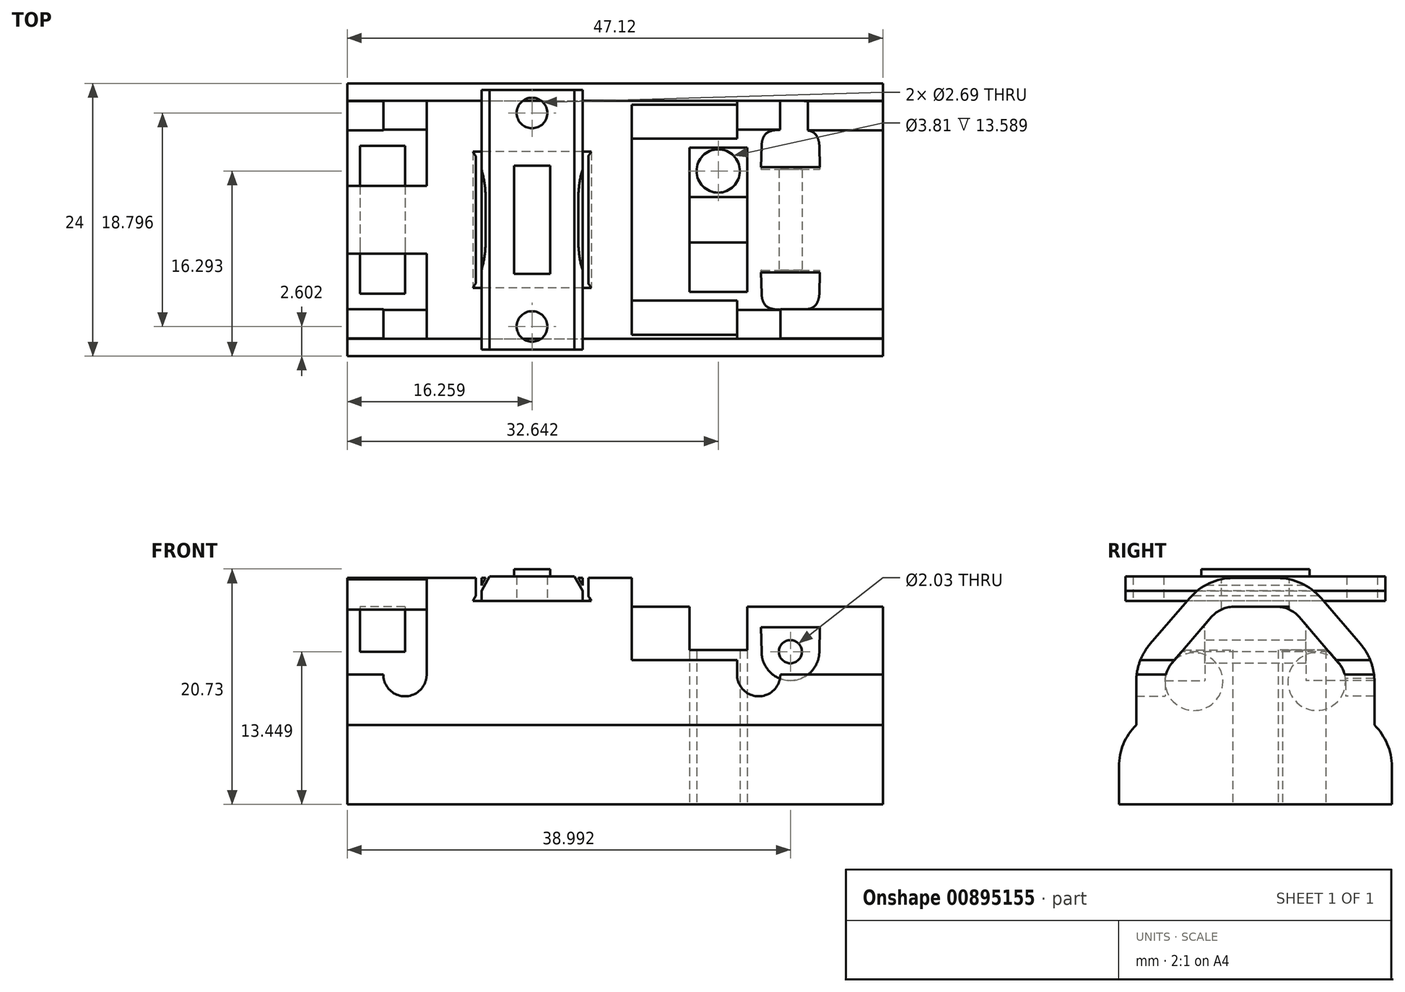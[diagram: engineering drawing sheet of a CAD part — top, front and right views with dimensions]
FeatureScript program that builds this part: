
annotation { "Feature Type Name" : "Feature", "Feature Type Description" : "" }
export const myFeature = defineFeature(function(context is Context, id is Id, definition is map)
    precondition{}
    {
        {
            var Q0;
            Q0=qCreatedBy(makeId("Right.planeOp"),FACE);
            var sketch = newSketch(context, id + "F0", { "sketchPlane" : qUnion([Q0])});
            skLineSegment(sketch, "E0.bottom", {"start": v(0, 0) * mm, "end": v(12, 0) * mm});
            skLineSegment(sketch, "E0.top", {"start": v(10.48, 6.99) * mm, "end": v(12, 6.99) * mm});
            skLineSegment(sketch, "E0.left", {"start": v(0, 0) * mm, "end": v(0, 6.99) * mm});
            skLineSegment(sketch, "E0.right", {"start": v(12, 0) * mm, "end": v(12, 6.99) * mm});
            skLineSegment(sketch, "E1.bottom", {"start": v(0, 0) * mm, "end": v(10.48, 0) * mm});
            skLineSegment(sketch, "E1.top", {"start": v(0, 19.94) * mm, "end": v(4.25, 19.94) * mm});
            skLineSegment(sketch, "E1.left", {"start": v(0, 0) * mm, "end": v(0, 19.94) * mm});
            skLineSegment(sketch, "E1.right", {"start": v(10.48, 6.99) * mm, "end": v(10.48, 12.7) * mm});
            skLineSegment(sketch, "E2", {"start": v(4.25, 19.94) * mm, "end": v(10.48, 12.7) * mm});
            skSolve(sketch);
        }
        {
            var Q0;
            Q0=qSketchRegion(id+"F0",true);
            extrude(context, id + "F1", {"entities" : qUnion([Q0]), "oppositeDirection" : true, "depth" : 47.12 * mm, "offsetDistance" : 25.4 * mm});
        }
        {
            var Q0;
            Q0=makeQuery(id+"F1.opExtrude","SWEPT_EDGE",EDGE,{"disambiguationData":[OSD([sQuery(id+"F0.wireOp",EDGE,"E1.top"),sQuery(id+"F0.wireOp",EDGE,"E2")])]});
            var Q1;
            Q1=makeQuery(id+"F1.opExtrude","SWEPT_EDGE",EDGE,{"disambiguationData":[OSD([sQuery(id+"F0.wireOp",EDGE,"E1.right"),sQuery(id+"F0.wireOp",EDGE,"E2")])]});
            var Q2;
            Q2=makeQuery(id+"F1.opExtrude","SWEPT_EDGE",EDGE,{"disambiguationData":[OSD([sQuery(id+"F0.wireOp",EDGE,"E0.top"),sQuery(id+"F0.wireOp",EDGE,"E0.right")])]});
            fillet(context, id + "F2", {"entities" : qUnion([Q0, Q1, Q2]), "radius" : 5.08 * mm, "tangentPropagation" : true, "allowEdgeOverflow" : false});
        }
        {
            var Q0;
            Q0=makeQuery(id+"F1.opExtrude","CAP_FACE",FACE,{"disambiguationData":[OSD([sQuery(id+"F0.wireOp",EDGE,"E0.bottom"),sQuery(id+"F0.wireOp",EDGE,"E0.top"),sQuery(id+"F0.wireOp",EDGE,"E0.right"),sQuery(id+"F0.wireOp",EDGE,"E1.bottom"),sQuery(id+"F0.wireOp",EDGE,"E1.top"),sQuery(id+"F0.wireOp",EDGE,"E1.left"),sQuery(id+"F0.wireOp",EDGE,"E1.right"),sQuery(id+"F0.wireOp",EDGE,"E2")])],"isStart":true});
            var Q1;
            Q1=makeQuery(id+"F1.opExtrude","SWEPT_FACE",FACE,{"disambiguationData":[OSD([sQuery(id+"F0.wireOp",EDGE,"E1.left")])]});
            var Q2;
            Q2=makeQuery(id+"F1.opExtrude","CAP_FACE",FACE,{"disambiguationData":[OSD([sQuery(id+"F0.wireOp",EDGE,"E0.bottom"),sQuery(id+"F0.wireOp",EDGE,"E0.top"),sQuery(id+"F0.wireOp",EDGE,"E0.right"),sQuery(id+"F0.wireOp",EDGE,"E1.bottom"),sQuery(id+"F0.wireOp",EDGE,"E1.top"),sQuery(id+"F0.wireOp",EDGE,"E1.left"),sQuery(id+"F0.wireOp",EDGE,"E1.right"),sQuery(id+"F0.wireOp",EDGE,"E2")])],"isStart":false});
            var Q3;
            Q3=makeQuery(id+"F1.opExtrude","SWEPT_FACE",FACE,{"disambiguationData":[OSD([sQuery(id+"F0.wireOp",EDGE,"E0.bottom"),sQuery(id+"F0.wireOp",EDGE,"E1.bottom")])]});
            shell(context, id + "F3", {"entities" : qUnion([Q0, Q1, Q2, Q3]), "thickness" : 2.54 * mm});
        }
        {
            var Q0;
            Q0=qCreatedBy(makeId("Front.planeOp"),FACE);
            var sketch = newSketch(context, id + "F4", { "sketchPlane" : qUnion([Q0])});
            skLineSegment(sketch, "E3.bottom", {"start": v(0, 12.7) * mm, "end": v(-22.1, 12.7) * mm});
            skLineSegment(sketch, "E3.top", {"start": v(0, 25.4) * mm, "end": v(-22.1, 25.4) * mm});
            skLineSegment(sketch, "E3.left", {"start": v(0, 12.7) * mm, "end": v(0, 25.4) * mm});
            skLineSegment(sketch, "E3.right", {"start": v(-22.1, 12.7) * mm, "end": v(-22.1, 25.4) * mm});
            skSolve(sketch);
        }
        {
            var Q0;
            Q0=qSketchRegion(id+"F4",true);
            extrude(context, id + "F5", {"entities" : qUnion([Q0]), "operationType" : NewBodyOperationType.REMOVE, "oppositeDirection" : true, "depth" : 25.4 * mm, "offsetDistance" : 25.4 * mm});
        }
        {
            var Q0;
            Q0=qCreatedBy(makeId("Front.planeOp"),FACE);
            var sketch = newSketch(context, id + "F6", { "sketchPlane" : qUnion([Q0])});
            skArc(sketch, "E4", {"start": v(-12.83, 11.43) * mm, "mid": v(-10.92, 9.53) * mm, "end": v(-9.02, 11.43) * mm});
            skLineSegment(sketch, "E5.bottom", {"start": v(-9.02, 11.43) * mm, "end": v(0, 11.43) * mm});
            skLineSegment(sketch, "E5.top", {"start": v(-10.92, 17.78) * mm, "end": v(0, 17.78) * mm});
            skLineSegment(sketch, "E5.left", {"start": v(-10.92, 13.34) * mm, "end": v(-10.92, 17.78) * mm});
            skLineSegment(sketch, "E5.right", {"start": v(0, 11.43) * mm, "end": v(0, 17.78) * mm});
            skLineSegment(sketch, "E6", {"start": v(-10.92, 17.78) * mm, "end": v(-12.83, 17.78) * mm});
            skLineSegment(sketch, "E7", {"start": v(-12.83, 17.78) * mm, "end": v(-12.83, 11.43) * mm});
            skSolve(sketch);
        }
        {
            var Q0;
            Q0=qSketchRegion(id+"F6",true);
            extrude(context, id + "F7", {"entities" : qUnion([Q0]), "operationType" : NewBodyOperationType.REMOVE, "oppositeDirection" : true, "depth" : 25.4 * mm, "offsetDistance" : 25.4 * mm});
        }
        {
            var Q0;
            Q0=qCreatedBy(makeId("Front.planeOp"),FACE);
            cPlane(context, id + "F8", {"entities" : qUnion([Q0]), "cplaneType" : CPlaneType.OFFSET, "offset" : 2.98 * mm, "oppositeDirection" : true, "width" : 152.4 * mm, "height" : 152.4 * mm});
        }
        {
            var Q0;
            Q0=qCreatedBy(id+"F8.planeOp",FACE);
            var sketch = newSketch(context, id + "F9", { "sketchPlane" : qUnion([Q0])});
            skPoint(sketch, "E8.0", {"position": v(-10.92, 9.53) * mm});
            skLineSegment(sketch, "E9.0", {"start": v(0, 11.43) * mm, "end": v(-9.02, 11.43) * mm});
            skArc(sketch, "E10.0", {"start": v(-9.12, 10.82) * mm, "mid": v(-10.92, 9.53) * mm, "end": v(-12.73, 10.82) * mm});
            skArc(sketch, "E11", {"start": v(-43.94, 11.43) * mm, "mid": v(-42.04, 9.53) * mm, "end": v(-40.13, 11.43) * mm});
            skPoint(sketch, "E12.0", {"position": v(-47.12, 18.67) * mm});
            skLineSegment(sketch, "E13.0", {"start": v(-47.12, 17.4) * mm, "end": v(-47.12, 19.94) * mm});
            skLineSegment(sketch, "E14.bottom", {"start": v(-43.94, 11.43) * mm, "end": v(-47.12, 11.43) * mm});
            skLineSegment(sketch, "E14.top", {"start": v(-42.04, 19.94) * mm, "end": v(-47.12, 19.94) * mm});
            skLineSegment(sketch, "E14.left", {"start": v(-42.04, 11.43) * mm, "end": v(-42.04, 19.94) * mm});
            skLineSegment(sketch, "E14.right", {"start": v(-47.12, 11.43) * mm, "end": v(-47.12, 19.94) * mm});
            skLineSegment(sketch, "E15.top", {"start": v(-42.04, 19.94) * mm, "end": v(-40.13, 19.94) * mm});
            skLineSegment(sketch, "E15.right", {"start": v(-40.13, 11.43) * mm, "end": v(-40.13, 19.94) * mm});
            skSolve(sketch);
        }
        {
            var Q0;
            Q0=qSketchRegion(id+"F9",true);
            extrude(context, id + "F10", {"entities" : qUnion([Q0]), "operationType" : NewBodyOperationType.REMOVE, "oppositeDirection" : true, "depth" : 25.4 * mm, "offsetDistance" : 25.4 * mm});
        }
        {
            var Q0;
            Q0=qCreatedBy(makeId("Front.planeOp"),FACE);
            var sketch = newSketch(context, id + "F11", { "sketchPlane" : qUnion([Q0])});
            skLineSegment(sketch, "E16.0", {"start": v(-47.12, 19.94) * mm, "end": v(-22.1, 19.94) * mm});
            skLineSegment(sketch, "E17.0", {"start": v(-22.1, 17.4) * mm, "end": v(-22.1, 19.94) * mm});
            skLineSegment(sketch, "E18", {"start": v(-25.65, 17.9) * mm, "end": v(-36.07, 17.9) * mm});
            skLineSegment(sketch, "E19", {"start": v(-36.07, 17.9) * mm, "end": v(-34.94, 19.94) * mm});
            skLineSegment(sketch, "E20", {"start": v(-34.94, 19.94) * mm, "end": v(-26.78, 19.94) * mm});
            skLineSegment(sketch, "E21", {"start": v(-26.78, 19.94) * mm, "end": v(-25.65, 17.9) * mm});
            skLineSegment(sketch, "E22.0", {"start": v(0, 5.69) * mm, "end": v(0, 10.82) * mm});
            skSolve(sketch);
        }
        {
            var Q0;
            Q0=qSketchRegion(id+"F11",true);
            extrude(context, id + "F12", {"entities" : qUnion([Q0]), "operationType" : NewBodyOperationType.REMOVE, "oppositeDirection" : true, "depth" : 25.4 * mm, "offsetDistance" : 25.4 * mm});
        }
        {
            var Q0;
            Q0=makeQuery(id+"F1.opExtrude","SWEPT_BODY",BODY,{"disambiguationData":[OSD([sQuery(id+"F0.wireOp",EDGE,"E0.bottom"),sQuery(id+"F0.wireOp",EDGE,"E0.top"),sQuery(id+"F0.wireOp",EDGE,"E0.right"),sQuery(id+"F0.wireOp",EDGE,"E1.bottom"),sQuery(id+"F0.wireOp",EDGE,"E1.top"),sQuery(id+"F0.wireOp",EDGE,"E1.left"),sQuery(id+"F0.wireOp",EDGE,"E1.right"),sQuery(id+"F0.wireOp",EDGE,"E2")])]});
            var Q1;
            Q1=qCreatedBy(makeId("Front.planeOp"),FACE);
            mirror(context, id + "F13", {"operationType" : NewBodyOperationType.ADD, "entities" : qUnion([Q0]), "mirrorPlane" : qUnion([Q1])});
        }
        {
            var Q0;
            Q0=qCreatedBy(makeId("Right.planeOp"),FACE);
            var sketch = newSketch(context, id + "F14", { "sketchPlane" : qUnion([Q0])});
            skLineSegment(sketch, "E23.0", {"start": v(1.92, 17.4) * mm, "end": v(0, 17.4) * mm});
            skArc(sketch, "E24.0", {"start": v(1.92, 17.4) * mm, "mid": v(2.98, 17.17) * mm, "end": v(3.85, 16.51) * mm});
            skLineSegment(sketch, "E25.0", {"start": v(7.13, 12.7) * mm, "end": v(3.85, 16.51) * mm});
            skArc(sketch, "E26.0", {"start": v(7.86, 11.43) * mm, "mid": v(7.65, 11.98) * mm, "end": v(7.32, 12.47) * mm});
            skLineSegment(sketch, "E27.0", {"start": v(7.13, 12.7) * mm, "end": v(7.32, 12.47) * mm});
            skArc(sketch, "E28.0", {"start": v(7.94, 10.82) * mm, "mid": v(7.92, 11.13) * mm, "end": v(7.86, 11.43) * mm});
            skLineSegment(sketch, "E29.0", {"start": v(7.94, 5.69) * mm, "end": v(7.94, 10.82) * mm});
            skArc(sketch, "E30.0", {"start": v(9.46, 3.36) * mm, "mid": v(9.05, 4.75) * mm, "end": v(7.94, 5.69) * mm});
            skLineSegment(sketch, "E31.0", {"start": v(9.46, 0) * mm, "end": v(9.46, 3.36) * mm});
            skLineSegment(sketch, "E32", {"start": v(9.46, 0) * mm, "end": v(0, 0) * mm});
            skLineSegment(sketch, "E33", {"start": v(0, 0) * mm, "end": v(0, 17.4) * mm});
            skPoint(sketch, "E34.orphan", {"position": v(-1.92, 17.4) * mm});
            skSolve(sketch);
        }
        {
            var Q0;
            Q0=qSketchRegion(id+"F14",true);
            var Q1;
            {var subQ0=sQuery(id+"F0.wireOp",EDGE,"E0.right");var subQ1=sQuery(id+"F0.wireOp",EDGE,"E0.top");var subQ2=sQuery(id+"F0.wireOp",EDGE,"E1.right");var subQ3=sQuery(id+"F0.wireOp",EDGE,"E1.bottom");var subQ4=sQuery(id+"F0.wireOp",EDGE,"E0.bottom");var subQ5=sQuery(id+"F0.wireOp",EDGE,"E2");Q1=makeQuery(id+"F10.boolean.opBoolean","SPLIT",FACE,{"disambiguationData":[TD([makeQuery(id+"F1.opExtrude","SWEPT_FACE",FACE,{"disambiguationData":[OSD([subQ0])]})])],"derivedFrom":makeQuery(id+"F1.opExtrude","CAP_FACE",FACE,{"disambiguationData":[OSD([subQ4,subQ1,subQ0,subQ3,sQuery(id+"F0.wireOp",EDGE,"E1.top"),sQuery(id+"F0.wireOp",EDGE,"E1.left"),subQ2,subQ5])],"isStart":false})});}
            extrude(context, id + "F15", {"entities" : qUnion([Q0]), "endBound" : BoundingType.UP_TO_SURFACE, "oppositeDirection" : true, "depth" : 25.4 * mm, "endBoundEntityFace" : qUnion([Q1]), "offsetDistance" : 25.4 * mm});
        }
        {
            var Q0;
            Q0=qCreatedBy(makeId("Front.planeOp"),FACE);
            var sketch = newSketch(context, id + "F16", { "sketchPlane" : qUnion([Q0])});
            skLineSegment(sketch, "E35.0", {"start": v(-40.13, 14.13) * mm, "end": v(-40.13, 18.17) * mm});
            skLineSegment(sketch, "E36.left", {"start": v(-46, 17.4) * mm, "end": v(-46, 13.44) * mm});
            skLineSegment(sketch, "E36.right", {"start": v(-42.04, 17.4) * mm, "end": v(-42.04, 13.44) * mm});
            skLineSegment(sketch, "E37.0", {"start": v(-46, 17.4) * mm, "end": v(-42.04, 17.4) * mm});
            skLineSegment(sketch, "E38", {"start": v(-46.1, 17.4) * mm, "end": v(-42.04, 17.4) * mm});
            skPoint(sketch, "E39.orphan", {"position": v(-47.12, 17.4) * mm});
            skLineSegment(sketch, "E40.trimOffspring", {"start": v(-40.13, 17.4) * mm, "end": v(0, 17.4) * mm});
            skLineSegment(sketch, "E41", {"start": v(-46, 13.44) * mm, "end": v(-42.04, 13.44) * mm});
            skSolve(sketch);
        }
        {
            var Q0;
            Q0=qSketchRegion(id+"F16",true);
            extrude(context, id + "F17", {"entities" : qUnion([Q0]), "operationType" : NewBodyOperationType.REMOVE, "oppositeDirection" : true, "depth" : 25.4 * mm, "offsetDistance" : 25.4 * mm});
        }
        {
            var Q0;
            Q0=qCreatedBy(makeId("Front.planeOp"),FACE);
            var sketch = newSketch(context, id + "F18", { "sketchPlane" : qUnion([Q0])});
            skLineSegment(sketch, "E42.bottom", {"start": v(-17.02, 19.94) * mm, "end": v(-11.94, 19.94) * mm});
            skLineSegment(sketch, "E42.top", {"start": v(-17.02, 13.59) * mm, "end": v(-11.94, 13.59) * mm});
            skLineSegment(sketch, "E42.left", {"start": v(-17.02, 19.94) * mm, "end": v(-17.02, 13.59) * mm});
            skLineSegment(sketch, "E42.right", {"start": v(-11.94, 19.94) * mm, "end": v(-11.94, 13.59) * mm});
            skSolve(sketch);
        }
        {
            var Q0;
            Q0=qSketchRegion(id+"F18",true);
            extrude(context, id + "F19", {"entities" : qUnion([Q0]), "operationType" : NewBodyOperationType.REMOVE, "oppositeDirection" : true, "depth" : 25.4 * mm, "offsetDistance" : 25.4 * mm});
        }
        {
            var Q0;
            Q0=qCreatedBy(makeId("Front.planeOp"),FACE);
            var sketch = newSketch(context, id + "F20", { "sketchPlane" : qUnion([Q0])});
            skCircle(sketch, "E43", {"center": v(-8.13, 13.45) * mm, "radius": 1.02 * mm});
            skSolve(sketch);
        }
        {
            var Q0;
            Q0=qSketchRegion(id+"F20",true);
            extrude(context, id + "F21", {"entities" : qUnion([Q0]), "operationType" : NewBodyOperationType.REMOVE, "oppositeDirection" : true, "depth" : 25.4 * mm, "offsetDistance" : 25.4 * mm});
        }
        {
            var Q0;
            Q0=qCreatedBy(makeId("Front.planeOp"),FACE);
            cPlane(context, id + "F22", {"entities" : qUnion([Q0]), "cplaneType" : CPlaneType.OFFSET, "offset" : 4.44 * mm, "oppositeDirection" : true, "width" : 152.4 * mm, "height" : 152.4 * mm});
        }
        {
            var Q0;
            Q0=qCreatedBy(id+"F22.planeOp",FACE);
            var sketch = newSketch(context, id + "F23", { "sketchPlane" : qUnion([Q0])});
            skCircle(sketch, "E44.0", {"center": v(-8.13, 13.45) * mm, "radius": 1.02 * mm});
            skArc(sketch, "E45", {"start": v(-10.67, 13.4) * mm, "mid": v(-8.13, 10.9) * mm, "end": v(-5.59, 13.4) * mm});
            skLineSegment(sketch, "E46", {"start": v(-10.7, 15.6) * mm, "end": v(-5.55, 15.6) * mm});
            skLineSegment(sketch, "E47", {"start": v(-5.59, 13.4) * mm, "end": v(-5.55, 15.6) * mm});
            skLineSegment(sketch, "E48", {"start": v(-10.67, 13.4) * mm, "end": v(-10.7, 15.6) * mm});
            skSolve(sketch);
        }
        {
            var Q0;
            Q0=qSketchRegion(id+"F23",true);
            extrude(context, id + "F24", {"entities" : qUnion([Q0]), "operationType" : NewBodyOperationType.REMOVE, "oppositeDirection" : true, "depth" : 25.4 * mm, "offsetDistance" : 25.4 * mm});
        }
        {
            var Q0;
            Q0=qCreatedBy(makeId("Top.planeOp"),FACE);
            var sketch = newSketch(context, id + "F25", { "sketchPlane" : qUnion([Q0])});
            skLineSegment(sketch, "E49.0", {"start": v(-17.02, 6.36) * mm, "end": v(-11.94, 6.36) * mm});
            skLineSegment(sketch, "E50.0", {"start": v(-11.94, 1.92) * mm, "end": v(-11.94, 0) * mm});
            skLineSegment(sketch, "E51.0", {"start": v(-17.02, 1.92) * mm, "end": v(-17.02, 0) * mm});
            skLineSegment(sketch, "E52.0", {"start": v(-17.02, 0) * mm, "end": v(-11.94, 0) * mm});
            skLineSegment(sketch, "E53.bottom", {"start": v(-11.94, 0) * mm, "end": v(-17.02, 0) * mm});
            skLineSegment(sketch, "E53.top", {"start": v(-11.94, 2) * mm, "end": v(-17.02, 2) * mm});
            skLineSegment(sketch, "E53.left", {"start": v(-11.94, 0) * mm, "end": v(-11.94, 2) * mm});
            skLineSegment(sketch, "E53.right", {"start": v(-17.02, 0) * mm, "end": v(-17.02, 2) * mm});
            skSolve(sketch);
        }
        {
            var Q0;
            Q0=qSketchRegion(id+"F25",true);
            extrude(context, id + "F26", {"entities" : qUnion([Q0]), "operationType" : NewBodyOperationType.REMOVE, "depth" : 25.4 * mm, "offsetDistance" : 25.4 * mm});
        }
        {
            var Q0;
            Q0=makeQuery(id+"F15.opExtrude","SWEPT_BODY",BODY,{"disambiguationData":[OSD([sQuery(id+"F14.wireOp",EDGE,"E23.0"),sQuery(id+"F14.wireOp",EDGE,"E24.0"),sQuery(id+"F14.wireOp",EDGE,"E25.0"),sQuery(id+"F14.wireOp",EDGE,"E26.0"),sQuery(id+"F14.wireOp",EDGE,"E27.0"),sQuery(id+"F14.wireOp",EDGE,"E28.0"),sQuery(id+"F14.wireOp",EDGE,"E29.0"),sQuery(id+"F14.wireOp",EDGE,"E30.0"),sQuery(id+"F14.wireOp",EDGE,"E31.0"),sQuery(id+"F14.wireOp",EDGE,"E32"),sQuery(id+"F14.wireOp",EDGE,"E33")])]});
            var Q1;
            Q1=qCreatedBy(makeId("Front.planeOp"),FACE);
            mirror(context, id + "F27", {"operationType" : NewBodyOperationType.ADD, "entities" : qUnion([Q0]), "mirrorPlane" : qUnion([Q1])});
        }
        {
            var Q0;
            Q0=qCreatedBy(makeId("Top.planeOp"),FACE);
            var sketch = newSketch(context, id + "F28", { "sketchPlane" : qUnion([Q0])});
            skPoint(sketch, "E54.0", {"position": v(-14.48, 2) * mm});
            skCircle(sketch, "E55", {"center": v(-14.48, 4.3) * mm, "radius": 1.9 * mm});
            skSolve(sketch);
        }
        {
            var Q0;
            Q0=qSketchRegion(id+"F28",true);
            extrude(context, id + "F29", {"entities" : qUnion([Q0]), "operationType" : NewBodyOperationType.REMOVE, "depth" : 25.4 * mm, "offsetDistance" : 25.4 * mm});
        }
        {
            var Q0;
            Q0=qCreatedBy(makeId("Front.planeOp"),FACE);
            var sketch = newSketch(context, id + "F30", { "sketchPlane" : qUnion([Q0])});
            skLineSegment(sketch, "E56.0", {"start": v(-26.03, 17.9) * mm, "end": v(-35.59, 17.9) * mm});
            skLineSegment(sketch, "E57.0", {"start": v(-34.94, 19.94) * mm, "end": v(-35.85, 18.3) * mm});
            skLineSegment(sketch, "E58.0", {"start": v(-22.1, 19.94) * mm, "end": v(-26.78, 19.94) * mm});
            skLineSegment(sketch, "E59", {"start": v(-35.81, 17.9) * mm, "end": v(-25.9, 17.9) * mm});
            skLineSegment(sketch, "E60", {"start": v(-27.12, 20.1) * mm, "end": v(-34.6, 20.1) * mm});
            skLineSegment(sketch, "E61", {"start": v(-34.86, 20.1) * mm, "end": v(-36.07, 17.9) * mm});
            skLineSegment(sketch, "E62", {"start": v(-26.86, 20.1) * mm, "end": v(-25.65, 17.9) * mm});
            skLineSegment(sketch, "E63.0", {"start": v(0, 11.43) * mm, "end": v(-9.02, 11.43) * mm});
            skLineSegment(sketch, "E64", {"start": v(-27.12, 20.1) * mm, "end": v(-25.9, 17.9) * mm});
            skLineSegment(sketch, "E65", {"start": v(-34.6, 20.1) * mm, "end": v(-35.81, 17.9) * mm});
            skSolve(sketch);
        }
        {
            var Q0;
            {var subQ2=sQuery(id+"F30.wireOp",EDGE,"E60");Q0=makeQuery(id+"F30.imprint","IMPRINT",FACE,{"disambiguationData":[TD([[makeQuery(id+"F30.imprint","IMPRINT",EDGE,{"derivedFrom":subQ2}),1.0]])]});}
            extrude(context, id + "F31", {"entities" : qUnion([Q0]), "endBound" : BoundingType.SYMMETRIC, "depth" : 22.86 * mm, "offsetDistance" : 25.4 * mm});
        }
        {
            var Q0;
            Q0=qCreatedBy(makeId("Front.planeOp"),FACE);
            var sketch = newSketch(context, id + "F32", { "sketchPlane" : qUnion([Q0])});
            skLineSegment(sketch, "E66.0", {"start": v(-27.12, 20.1) * mm, "end": v(-27.12, 20.1) * mm});
            skLineSegment(sketch, "E67", {"start": v(-30.86, 20.1) * mm, "end": v(-30.86, 20.73) * mm, "construction": true});
            skLineSegment(sketch, "E68.bottom", {"start": v(-30.86, 20.73) * mm, "end": v(-32.45, 20.73) * mm});
            skLineSegment(sketch, "E68.top", {"start": v(-30.86, 20.1) * mm, "end": v(-32.45, 20.1) * mm});
            skLineSegment(sketch, "E68.left", {"start": v(-30.86, 20.73) * mm, "end": v(-30.86, 20.1) * mm});
            skLineSegment(sketch, "E68.right", {"start": v(-32.45, 20.73) * mm, "end": v(-32.45, 20.1) * mm});
            skLineSegment(sketch, "E69.MirrorCS", {"start": v(-29.27, 20.73) * mm, "end": v(-29.27, 20.1) * mm});
            skLineSegment(sketch, "E70.MirrorCS", {"start": v(-30.86, 20.73) * mm, "end": v(-29.27, 20.73) * mm});
            skLineSegment(sketch, "E71.MirrorCS", {"start": v(-30.86, 20.1) * mm, "end": v(-29.27, 20.1) * mm});
            skSolve(sketch);
        }
        {
            var Q0;
            Q0=makeQuery(id+"F32.imprint","IMPRINT",FACE,{"disambiguationData":[TD([[makeQuery(id+"F32.imprint","IMPRINT",EDGE,{"derivedFrom":sQuery(id+"F32.wireOp",EDGE,"E68.bottom")}),1.0]])]});
            var Q1;
            Q1=makeQuery(id+"F32.imprint","IMPRINT",FACE,{"disambiguationData":[TD([[makeQuery(id+"F32.imprint","IMPRINT",EDGE,{"derivedFrom":sQuery(id+"F32.wireOp",EDGE,"E68.left")}),1.0]])]});
            extrude(context, id + "F33", {"entities" : qUnion([Q0, Q1]), "operationType" : NewBodyOperationType.ADD, "endBound" : BoundingType.SYMMETRIC, "depth" : 9.52 * mm, "offsetDistance" : 25.4 * mm});
        }
        {
            var Q0;
            {var subQ0=makeQuery(id+"F17.boolean.opBoolean","COPY",FACE,{"derivedFrom":makeQuery(id+"F17.opExtrude","SWEPT_FACE",FACE,{"disambiguationData":[OSD([sQuery(id+"F16.wireOp",EDGE,"E36.left")])]})});Q0=makeQuery(id+"F27.boolean.opBoolean","MERGE",FACE,{"derivedFrom":[subQ0,makeQuery(id+"F27.opPattern","COPY",FACE,{"derivedFrom":subQ0,"instanceName":"1"})]});}
            cPlane(context, id + "F34", {"entities" : qUnion([Q0]), "cplaneType" : CPlaneType.OFFSET, "offset" : 2.08 * mm, "width" : 152.4 * mm, "height" : 152.4 * mm});
        }
        {
            var Q0;
            Q0=qCreatedBy(makeId("Front.planeOp"),FACE);
            var sketch = newSketch(context, id + "F35", { "sketchPlane" : qUnion([Q0])});
            skLineSegment(sketch, "E72.0", {"start": v(-35.81, 17.9) * mm, "end": v(-25.9, 17.9) * mm});
            skLineSegment(sketch, "E73.0", {"start": v(-27.12, 20.1) * mm, "end": v(-34.6, 20.1) * mm});
            skLineSegment(sketch, "E74", {"start": v(-30.86, 20.1) * mm, "end": v(-30.86, 17.9) * mm, "construction": true});
            skLineSegment(sketch, "E75.bottom", {"start": v(-25.9, 17.9) * mm, "end": v(-26.42, 17.9) * mm});
            skLineSegment(sketch, "E75.top", {"start": v(-25.9, 20.1) * mm, "end": v(-26.42, 20.1) * mm});
            skLineSegment(sketch, "E75.left", {"start": v(-25.9, 17.9) * mm, "end": v(-25.9, 20.1) * mm});
            skLineSegment(sketch, "E75.right", {"start": v(-26.42, 17.9) * mm, "end": v(-26.42, 20.1) * mm});
            skLineSegment(sketch, "E76.MirrorCS", {"start": v(-35.3, 17.9) * mm, "end": v(-35.3, 20.1) * mm});
            skLineSegment(sketch, "E77.MirrorCS", {"start": v(-35.81, 20.1) * mm, "end": v(-35.3, 20.1) * mm});
            skLineSegment(sketch, "E78.MirrorCS", {"start": v(-35.81, 17.9) * mm, "end": v(-35.81, 20.1) * mm});
            skSolve(sketch);
        }
        {
            var Q0;
            Q0 = qSketchRegion(id + "F35", true);
            extrude(context, id + "F36", {"entities" : qUnion([Q0]), "operationType" : NewBodyOperationType.REMOVE, "endBound" : BoundingType.SYMMETRIC, "oppositeDirection" : true, "depth" : 25.4 * mm, "offsetDistance" : 25.4 * mm});
        }
        {
            var Q0;
            Q0=makeQuery(id+"F31.opExtrude","SWEPT_FACE",FACE,{"disambiguationData":[OSD([sQuery(id+"F30.wireOp",EDGE,"E59")])]});
            var sketch = newSketch(context, id + "F37", { "sketchPlane" : qUnion([Q0])});
            skLineSegment(sketch, "E79.0", {"start": v(-27.12, 11.43) * mm, "end": v(-27.12, -11.43) * mm});
            skLineSegment(sketch, "E80.0", {"start": v(-27.12, 11.43) * mm, "end": v(-34.6, 11.43) * mm});
            skLineSegment(sketch, "E81", {"start": v(-30.86, -11.43) * mm, "end": v(-30.86, 11.43) * mm, "construction": true});
            skLineSegment(sketch, "E82", {"start": v(-27.12, 0) * mm, "end": v(-34.6, 0) * mm, "construction": true});
            skCircle(sketch, "E83", {"center": v(-30.86, -9.4) * mm, "radius": 1.35 * mm});
            skCircle(sketch, "E84.MirrorC", {"center": v(-30.86, 9.4) * mm, "radius": 1.35 * mm});
            skSolve(sketch);
        }
        {
            var Q0;
            Q0 = qSketchRegion(id + "F37", true);
            extrude(context, id + "F38", {"entities" : qUnion([Q0]), "operationType" : NewBodyOperationType.REMOVE, "oppositeDirection" : true, "depth" : 25.4 * mm, "offsetDistance" : 25.4 * mm});
        }
    });
